# Revit family: Valve-Bath_and_Shower-KOHLER-KOHLER-K-882M
name_source: partatom
category: Plumbing Fixtures
revit_build: Autodesk Revit 2017 (Build: 20160225_1515(x64)
units: mm (PartAtom-declared; Revit-internal decimal feet)

## family parameters
Cut with Voids When Loaded = No
Host = Face
OmniClass Number = 23.27.31.00
OmniClass Title = Valves
Part Type = Normal
Room Calculation Point = No
Round Connector Dimension = Use Diameter
Shared = No

## types (1)
- CP-Polished Chrome
    ADA Compliant = No
    Assembly Code = D2020
    CW Connection = Yes
    Cold Water Inlet = Cold Water Inlet
    Date Modified = 11/13/2020
    Default Elevation = 36"
    Description = 40mm bath and shower valve with diverter
    Finish = Kohler-Metal-CP-Polished_Chrome
    Flow Rate = 11 GPM
    HW Connection = Yes
    Height = 6 5/16"
    Hot Water Inlet = Hot Water Inlet
    Length = 5 3/8"
    Manufacturer = KOHLER Co.
    MasterFormat 1995 = 154300
    MasterFormat 2004 = 22.11.00
    Material = Solid Brass Construction
    Model = K-882M-CP
    Pressure = 60.00 psi
    Product Documentation Link = http://resources.kohler.com
    Product Name = KOHLER
    Product Page URL = https://la.kohler.com
    Tempered Water Outlet 1 = Tempered Water Outlet 1
    Tempered Water Outlet 2 = Tempered Water Outlet 2
    URL = https://la.kohler.com
    Vent Connection = No
    Waste Connection = No
    Waste Water Outlet = Waste Water Outlet
    WaterSense Certified = No
    Width = 3 7/16"

## geometry (parser evidence)
native form markers: Sweep x4
no freeform markers — native parametric forms only
